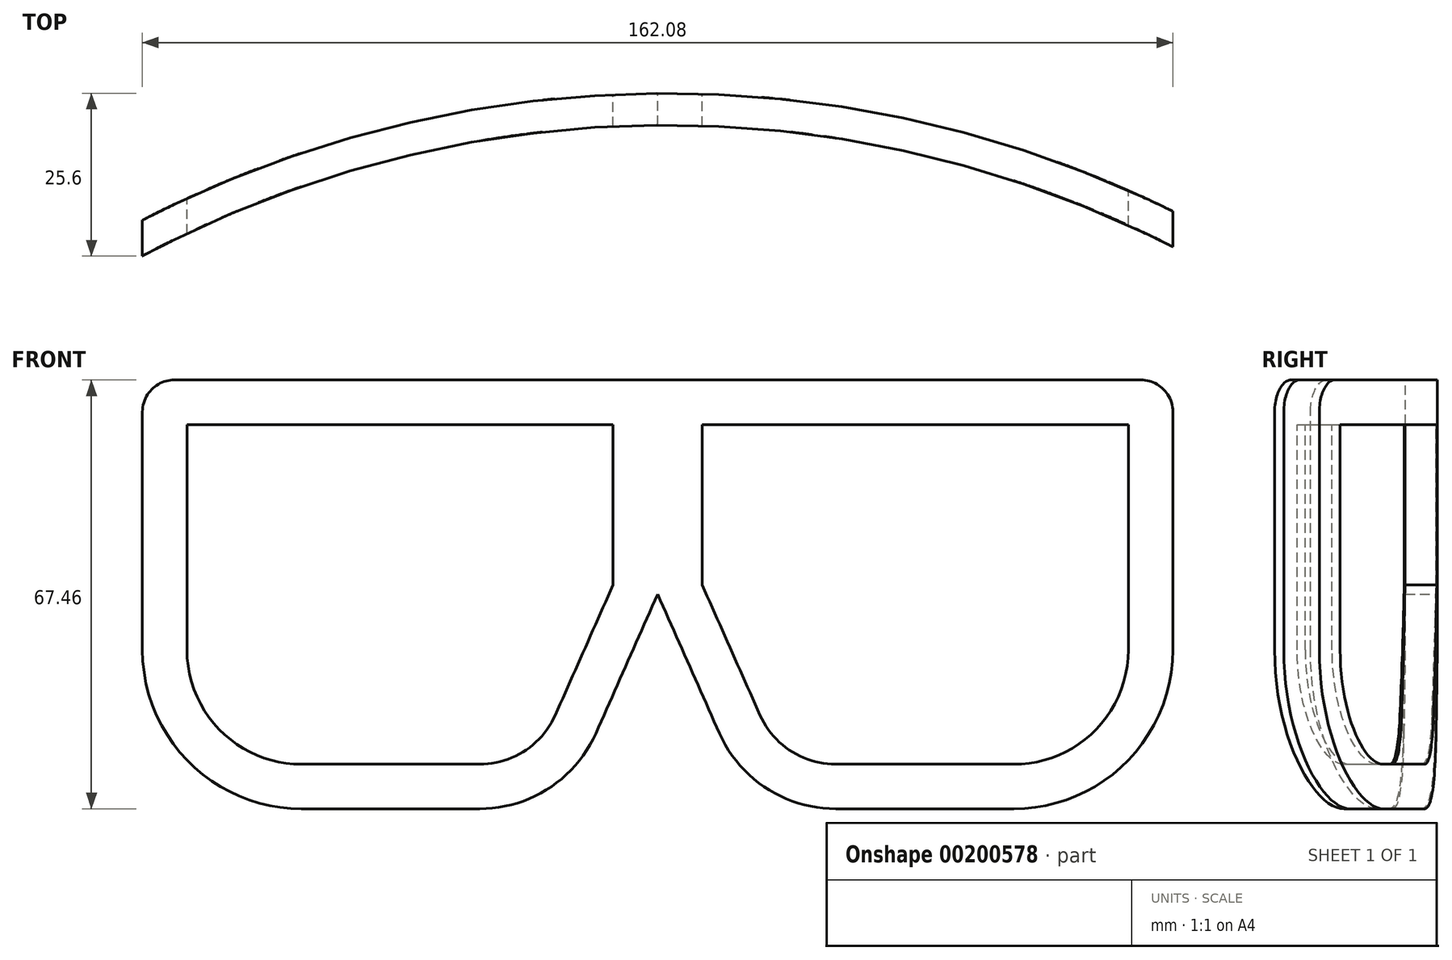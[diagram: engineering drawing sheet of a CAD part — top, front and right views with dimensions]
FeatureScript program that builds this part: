
annotation { "Feature Type Name" : "Feature", "Feature Type Description" : "" }
export const myFeature = defineFeature(function(context is Context, id is Id, definition is map)
    precondition{}
    {
        {
            var Q0;
            Q0=qCreatedBy(makeId("Front.planeOp"),FACE);
            var sketch = newSketch(context, id + "F0", { "sketchPlane" : qUnion([Q0])});
            skLineSegment(sketch, "E0.right", {"start": v(-81.04, -8.73) * mm, "end": v(-81.04, 28.73) * mm});
            skPoint(sketch, "E0.middle", {"position": v(0, 0) * mm});
            skLineSegment(sketch, "E1.trimOffspring", {"start": v(0, 33.73) * mm, "end": v(-76.04, 33.73) * mm});
            skLineSegment(sketch, "E2.trimOffspring", {"start": v(-28, -33.73) * mm, "end": v(-56.04, -33.73) * mm});
            skPoint(sketch, "E0.left.end.orphan", {"position": v(81.04, 33.73) * mm});
            skPoint(sketch, "E0.left.start.orphan", {"position": v(81.04, -33.73) * mm});
            skLineSegment(sketch, "E3", {"start": v(0, 0) * mm, "end": v(-9.72, -21.86) * mm});
            skPoint(sketch, "E4.orphan", {"position": v(0, -33.73) * mm});
            skPoint(sketch, "E5.visualSharp", {"position": v(-15, -33.73) * mm});
            skArc(sketch, "E5.filletArc", {"start": v(-28, -33.73) * mm, "mid": v(-17.1, -30.5) * mm, "end": v(-9.72, -21.86) * mm});
            skPoint(sketch, "E6.visualSharp", {"position": v(-81.04, 33.73) * mm});
            skArc(sketch, "E6.filletArc", {"start": v(-76.04, 33.73) * mm, "mid": v(-79.57, 32.26) * mm, "end": v(-81.04, 28.73) * mm});
            skPoint(sketch, "E7.visualSharp", {"position": v(-81.04, -33.73) * mm});
            skArc(sketch, "E7.filletArc", {"start": v(-81.04, -8.73) * mm, "mid": v(-73.72, -26.4) * mm, "end": v(-56.04, -33.73) * mm});
            skLineSegment(sketch, "E8.0", {"start": v(-7, 1.49) * mm, "end": v(-7, 26.73) * mm});
            skLineSegment(sketch, "E8.1", {"start": v(-7, 1.49) * mm, "end": v(-16.12, -19.01) * mm});
            skLineSegment(sketch, "E8.2", {"start": v(-74.04, -8.73) * mm, "end": v(-74.04, 26.73) * mm});
            skArc(sketch, "E8.3", {"start": v(-74.04, -8.73) * mm, "mid": v(-68.77, -21.46) * mm, "end": v(-56.04, -26.73) * mm});
            skLineSegment(sketch, "E8.4", {"start": v(-28, -26.73) * mm, "end": v(-56.04, -26.73) * mm});
            skLineSegment(sketch, "E8.5", {"start": v(-7, 26.73) * mm, "end": v(-74.04, 26.73) * mm});
            skArc(sketch, "E8.6", {"start": v(-28, -26.73) * mm, "mid": v(-20.91, -24.63) * mm, "end": v(-16.12, -19.01) * mm});
            skLineSegment(sketch, "E9.MirrorCS", {"start": v(7, 26.73) * mm, "end": v(74.04, 26.73) * mm});
            skArc(sketch, "E10.MirrorCS", {"start": v(28, -26.73) * mm, "mid": v(20.91, -24.63) * mm, "end": v(16.12, -19.01) * mm});
            skLineSegment(sketch, "E11.MirrorCS", {"start": v(28, -33.73) * mm, "end": v(56.04, -33.73) * mm});
            skArc(sketch, "E12.MirrorCS", {"start": v(76.04, 33.73) * mm, "mid": v(79.57, 32.26) * mm, "end": v(81.04, 28.73) * mm});
            skArc(sketch, "E13.MirrorCS", {"start": v(81.04, -8.73) * mm, "mid": v(73.72, -26.4) * mm, "end": v(56.04, -33.73) * mm});
            skArc(sketch, "E14.MirrorCS", {"start": v(28, -33.73) * mm, "mid": v(17.1, -30.5) * mm, "end": v(9.72, -21.86) * mm});
            skLineSegment(sketch, "E15.MirrorCS", {"start": v(0, 0) * mm, "end": v(9.72, -21.86) * mm});
            skPoint(sketch, "E16.MirrorP", {"position": v(15, -33.73) * mm});
            skLineSegment(sketch, "E17.MirrorCS", {"start": v(7, 1.49) * mm, "end": v(7, 26.73) * mm});
            skLineSegment(sketch, "E18.MirrorCS", {"start": v(28, -26.73) * mm, "end": v(56.04, -26.73) * mm});
            skLineSegment(sketch, "E19.MirrorCS", {"start": v(81.04, -8.73) * mm, "end": v(81.04, 28.73) * mm});
            skLineSegment(sketch, "E20.MirrorCS", {"start": v(74.04, -8.73) * mm, "end": v(74.04, 26.73) * mm});
            skLineSegment(sketch, "E21.MirrorCS", {"start": v(0, 33.73) * mm, "end": v(76.04, 33.73) * mm});
            skLineSegment(sketch, "E22.MirrorCS", {"start": v(7, 1.49) * mm, "end": v(16.12, -19.01) * mm});
            skArc(sketch, "E23.MirrorCS", {"start": v(74.04, -8.73) * mm, "mid": v(68.77, -21.46) * mm, "end": v(56.04, -26.73) * mm});
            skSolve(sketch);
        }
        {
            var Q0;
            Q0 = qSketchRegion(id + "F0", true);
            extrude(context, id + "F1", {"entities" : qUnion([Q0]), "depth" : 50 * mm});
        }
        {
            var Q0;
            Q0=makeQuery(id+"F1.opExtrude","SWEPT_FACE",FACE,{"disambiguationData":[OSD([sQuery(id+"F0.wireOp",EDGE,"E1.trimOffspring"),sQuery(id+"F0.wireOp",EDGE,"E21.MirrorCS")])]});
            var sketch = newSketch(context, id + "F2", { "sketchPlane" : qUnion([Q0])});
            skPoint(sketch, "E24.endSnap0", {"position": v(0, -50) * mm});
            skArc(sketch, "E25", {"start": v(81.17, -26) * mm, "mid": v(-0.16, -7.4) * mm, "end": v(-81.15, -27.4) * mm});
            skArc(sketch, "E26.0", {"start": v(81.17, -31.6) * mm, "mid": v(-0.17, -12.4) * mm, "end": v(-81.15, -33.04) * mm});
            skLineSegment(sketch, "E27", {"start": v(-81.15, -33.04) * mm, "end": v(-81.15, -27.4) * mm});
            skLineSegment(sketch, "E28", {"start": v(81.17, -31.6) * mm, "end": v(81.17, -26) * mm});
            skSolve(sketch);
        }
        {
            var Q0;
            Q0 = qSketchRegion(id + "F2", true);
            extrude(context, id + "F3", {"entities" : qUnion([Q0]), "operationType" : NewBodyOperationType.INTERSECT, "oppositeDirection" : true, "depth" : 100 * mm});
        }
    });
